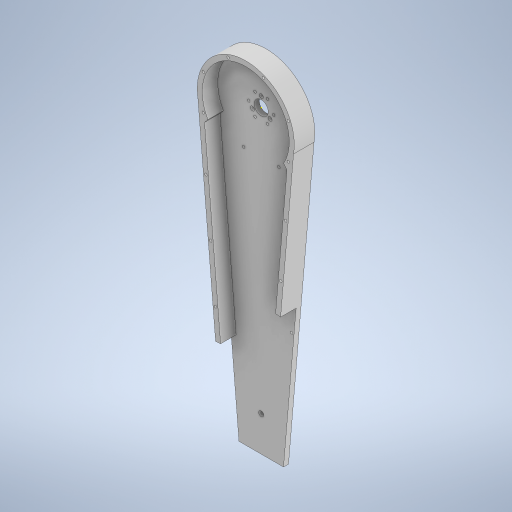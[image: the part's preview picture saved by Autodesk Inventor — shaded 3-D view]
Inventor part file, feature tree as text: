
AUTODESK INVENTOR PART (.ipt)
format: ipt  version: 2024.3 (Build 283343000, 343)  size: 404,480 bytes
history: native  units: mm
features: sketch x11, extrude x5, hole x5, other x1
ambient origin geometry x8: Origin, YZ Plane, XZ Plane, XY Plane, X Axis, Y Axis, Z Axis, Center Point
bodies: Body1 (feature_tree)
feature tree (22):
  other  "ソリッド1"
  extrude  "押し出し1"  Depth=97.0mm
  hole  "穴1"  [1 undecoded]
  extrude  "押し出し2"  Depth=20.5mm TaperAngle=0.0deg
  extrude  "押し出し3"  Depth=92.0mm
  extrude  "押し出し4"  TaperAngle=22.5deg  [1 undecoded]
  hole  "穴2"  [1 undecoded]
  hole  "穴3"  [1 undecoded]
  extrude  "押し出し9"  Depth=15.5mm TaperAngle=0.0deg
  hole  "穴4"  [1 undecoded]
  hole  "穴5"  [1 undecoded]
  sketch  "スケッチ15"
  sketch  "スケッチ1"
  sketch  "スケッチ2"
  sketch  "スケッチ3"
  sketch  "スケッチ4"
  sketch  "スケッチ5"
  sketch  "スケッチ6"
  sketch  "スケッチ7"
  sketch  "スケッチ12"
  sketch  "スケッチ13"
  sketch  "スケッチ14"
note: 6 required parameter values undecoded (feature->parameter linkage not recoverable at this tier; creation-order binding heuristic only, values carry confidence <= 0.55)
